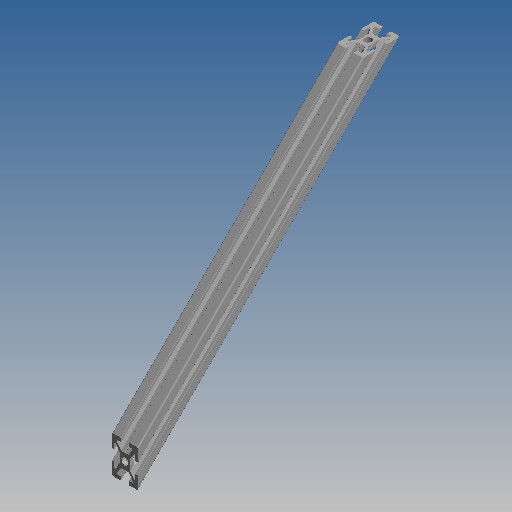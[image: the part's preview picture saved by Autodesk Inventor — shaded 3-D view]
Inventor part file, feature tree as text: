
AUTODESK INVENTOR PART (.ipt)
format: ipt  version: 2020 (Build 240168000, 168)  size: 310,272 bytes
history: native  units: mm (DEFAULTED — no unit token found)
features: other x14, sketch x5, extrude x3, revolve x2
ambient origin geometry x8: Origin, YZ Plane, XZ Plane, XY Plane, X Axis, Y Axis, Z Axis, Center Point
bodies: Solid1 (feature_tree)
feature tree (24):
  extrude  "Extrusion1"  Depth=800.0mm TaperAngle=0.0deg
  extrude  "Extrusion2"  TaperAngle=360.0deg  [1 undecoded]
  extrude  "Extrusion3"  TaperAngle=0.0deg  [1 undecoded]
  revolve  "Revolution1"  [1 undecoded]
  revolve  "Revolution2"  [1 undecoded]
  other  "bolt1_XY"
  other  "bolt1_YZ"
  other  "bolt1_ZX"
  other  "bolt1_X"
  other  "bolt1_Y"
  other  "bolt1_Z"
  other  "bolt1_Center"
  other  "bolt2_XY"
  other  "bolt2_YZ"
  other  "bolt2_ZX"
  other  "bolt2_X"
  other  "bolt2_Y"
  other  "bolt2_Z"
  other  "bolt2_Center"
  sketch  "Sketch_1"  dims[d0=284.842712mm d1=0.0mm d2=800.0mm d3=0.0mm]
  sketch  "Sketch_2"  dims[d4=800.0mm d5=0.0mm d6=360.0deg]
  sketch  "Sketch_3"  dims[d7=360.0deg d8=0.0mm d9=0.0mm]
  sketch  "Sketch_4"
  sketch  "Sketch_5"
note: 4 required parameter values undecoded (feature->parameter linkage not recoverable at this tier; creation-order binding heuristic only, values carry confidence <= 0.55)
